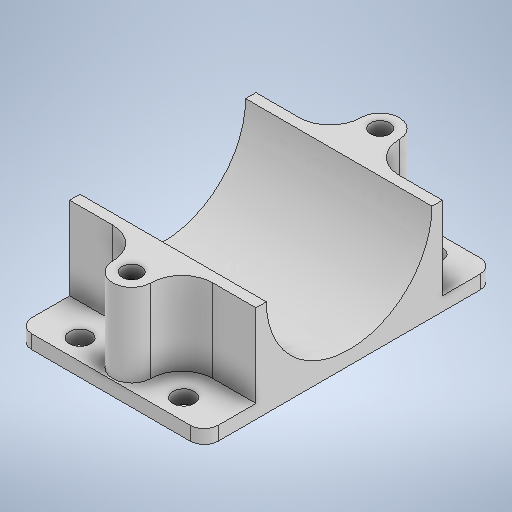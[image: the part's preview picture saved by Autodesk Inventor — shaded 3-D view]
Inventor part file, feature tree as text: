
AUTODESK INVENTOR PART (.ipt)
format: ipt  version: 2025.2 (Build 292293000, 293)  size: 316,416 bytes
history: native  units: mm
features: sketch x5, extrude x3, hole x2, other x1
ambient origin geometry x8: Origin, YZ Plane, XZ Plane, XY Plane, X Axis, Y Axis, Z Axis, Center Point
bodies: Body1 (feature_tree)
feature tree (11):
  other  "ソリッド1"
  extrude  "押し出し1"  Depth=27.0mm
  hole  "穴1"  [1 undecoded]
  extrude  "押し出し2"  Depth=2.0mm
  extrude  "押し出し3"  Depth=2.0mm TaperAngle=0.0deg
  hole  "穴2"  [1 undecoded]
  sketch  "スケッチ1"
  sketch  "スケッチ2"
  sketch  "スケッチ3"
  sketch  "スケッチ4"
  sketch  "スケッチ5"
note: 2 required parameter values undecoded (feature->parameter linkage not recoverable at this tier; creation-order binding heuristic only, values carry confidence <= 0.55)
